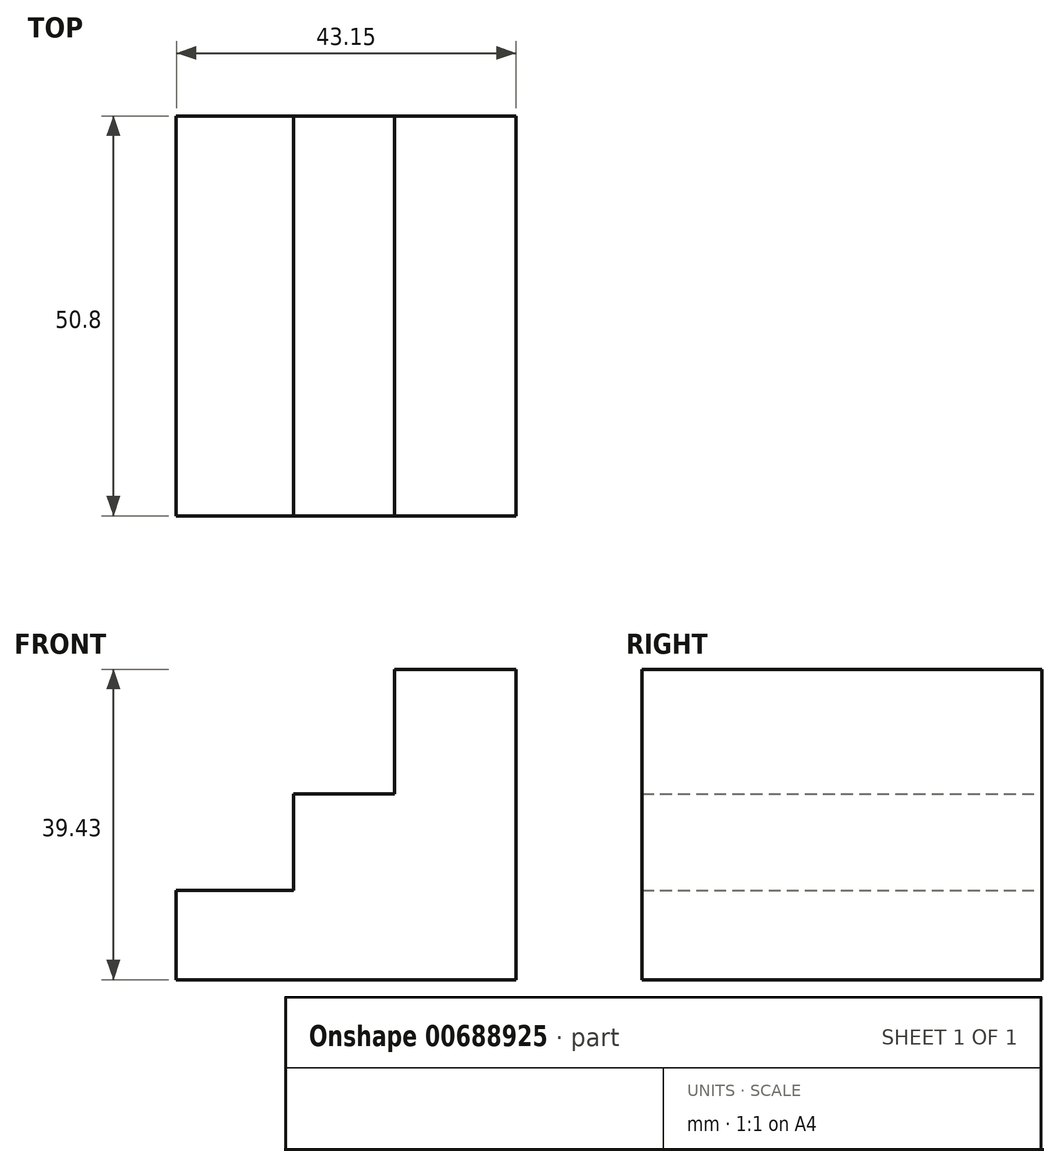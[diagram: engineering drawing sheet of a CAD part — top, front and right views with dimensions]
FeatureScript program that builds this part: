
annotation { "Feature Type Name" : "Feature", "Feature Type Description" : "" }
export const myFeature = defineFeature(function(context is Context, id is Id, definition is map)
    precondition{}
    {
        {
            var Q0;
            Q0=qCreatedBy(makeId("Front.planeOp"),FACE);
            var sketch = newSketch(context, id + "F0", { "sketchPlane" : qUnion([Q0])});
            skLineSegment(sketch, "E0", {"start": v(-35.42, 0) * mm, "end": v(-35.42, 11.36) * mm});
            skLineSegment(sketch, "E1", {"start": v(-35.42, 11.36) * mm, "end": v(-20.53, 11.36) * mm});
            skLineSegment(sketch, "E2", {"start": v(-20.53, 11.36) * mm, "end": v(-20.53, 23.58) * mm});
            skLineSegment(sketch, "E3", {"start": v(-20.53, 23.58) * mm, "end": v(-7.73, 23.58) * mm});
            skLineSegment(sketch, "E4", {"start": v(-7.73, 23.58) * mm, "end": v(-7.73, 39.43) * mm});
            skLineSegment(sketch, "E5", {"start": v(-7.73, 39.43) * mm, "end": v(7.73, 39.43) * mm});
            skLineSegment(sketch, "E6", {"start": v(7.73, 39.43) * mm, "end": v(7.73, 0) * mm});
            skLineSegment(sketch, "E7", {"start": v(7.73, 0) * mm, "end": v(-35.42, 0) * mm});
            skSolve(sketch);
        }
        {
            var Q0;
            Q0 = qSketchRegion(id + "F0", true);
            extrude(context, id + "F1", {"entities" : qUnion([Q0]), "depth" : 50.8 * mm, "offsetDistance" : 25.4 * mm});
        }
    });
